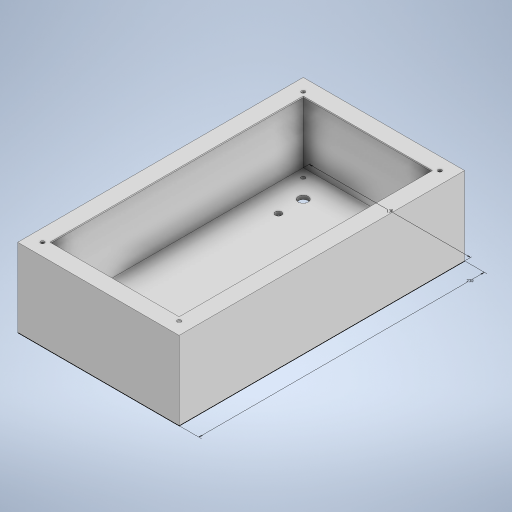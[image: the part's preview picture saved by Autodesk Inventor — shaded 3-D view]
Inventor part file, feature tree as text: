
AUTODESK INVENTOR PART (.ipt)
format: ipt  version: 2024 (Build 280153000, 153)  size: 352,256 bytes
history: native  units: mm
features: sketch x9, extrude x9, other x1
ambient origin geometry x8: Origin, YZ Plane, XZ Plane, XY Plane, X Axis, Y Axis, Z Axis, Center Point
bodies: Body1 (feature_tree)
feature tree (19):
  other  "Sólido1"
  sketch  "Boceto1"  dims[d0=130.0mm d1=230.0mm]
  extrude  "Extrusión1"  Depth=230.0mm
  extrude  "Extrusión2"  Depth=3.0mm
  extrude  "Extrusión3"  Depth=1.0mm
  extrude  "Extrusión4"  Depth=10.0mm
  extrude  "Extrusión5"  Depth=10.0mm TaperAngle=0.0deg
  extrude  "Extrusión6"  TaperAngle=0.0deg  [1 undecoded]
  extrude  "Extrusión7"  Depth=211.5mm TaperAngle=0.0deg
  extrude  "Extrusión8"  Depth=3.0mm
  extrude  "Extrusión9"  Depth=3.0mm
  sketch  "Boceto2"  dims[d2=3.0mm d3=0.0mm d4=3.0mm]
  sketch  "Boceto3"  dims[d5=60.0mm d6=0.0mm d7=1.0mm]
  sketch  "Boceto4"  dims[d8=10.0mm d9=0.0mm d10=10.0mm]
  sketch  "Boceto5"  dims[d11=10.0mm d12=115.25mm d13=0.0mm]
  sketch  "Boceto6"  dims[d14=10.0mm d15=0.0mm]
  sketch  "Boceto7"  dims[d16=0.0mm d17=211.5mm d18=0.0mm]
  sketch  "Boceto8"  dims[d19=3.0mm d20=3.0mm]
  sketch  "Boceto9"  dims[d21=3.0mm d22=3.0mm d23=10.0mm d24=10.0mm d25=10.0mm d26=10.0mm d27=10.0mm d28=10.0mm d29=10.0mm d30=10.0mm d31=211.5mm d32=0.0mm d33=8.0mm d34=8.0mm d35=8.0mm d36=8.0mm d37=25.0mm d38=25.0mm d39=25.0mm d40=25.0mm d41=25.0mm d42=25.0mm d43=25.0mm d44=25.0mm d45=10.0mm d46=0.0mm d47=70.0mm d48=10.0mm d49=35.0mm d50=30.0mm d51=30.0mm d52=5.0mm d53=5.0mm d54=5.0mm d55=5.0mm d56=5.0mm d57=5.0mm d58=10.0mm d59=0.0mm d60=90.0mm d61=130.0mm d62=20.0mm d63=20.0mm d64=60.0mm d65=5.0mm d66=5.0mm d67=5.0mm d68=5.0mm d69=5.0mm d70=5.0mm d71=5.0mm d72=5.0mm d73=5.0mm d74=5.0mm d75=5.0mm d76=5.0mm d77=10.0mm d78=0.0mm]
note: 1 required parameter value undecoded (feature->parameter linkage not recoverable at this tier; creation-order binding heuristic only, values carry confidence <= 0.55)
